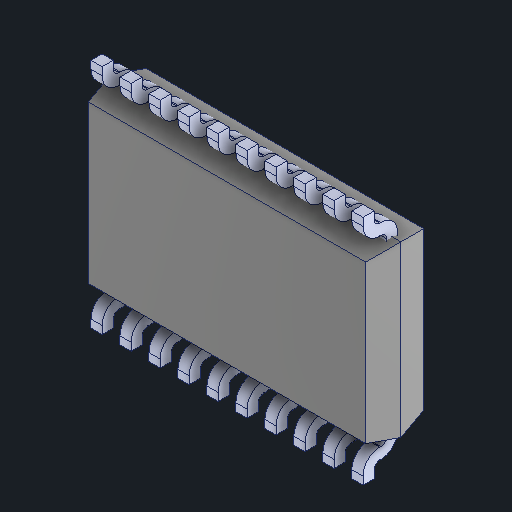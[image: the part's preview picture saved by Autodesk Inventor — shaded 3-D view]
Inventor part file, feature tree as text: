
AUTODESK INVENTOR PART (.ipt)
format: ipt  version: 2024 (Build 280153000, 153)  size: 306,688 bytes
history: native  units: mm
features: other x31, mirror x10, fillet x1
ambient origin geometry x8: Origin, YZ Plane, XZ Plane, XY Plane, X Axis, Y Axis, Z Axis, Center Point
bodies: Body1 (feature_tree), Body2 (feature_tree), Body3 (feature_tree), Body4 (feature_tree), Body5 (feature_tree), Body6 (feature_tree), Body7 (feature_tree), Body8 (feature_tree), Body9 (feature_tree), Body10 (feature_tree), Body11 (feature_tree), Body12 (feature_tree), Body13 (feature_tree), Body14 (feature_tree), Body15 (feature_tree), Body16 (feature_tree), Body17 (feature_tree), Body18 (feature_tree), Body19 (feature_tree), Body20 (feature_tree), Body21 (feature_tree)
feature tree (42):
  other  "Твердое тело1"
  other  "Твердое тело2"
  other  "Твердое тело3"
  other  "Твердое тело4"
  other  "Твердое тело5"
  other  "Твердое тело6"
  other  "Твердое тело7"
  other  "Твердое тело8"
  other  "Твердое тело9"
  other  "Твердое тело10"
  other  "Твердое тело11"
  other  "Твердое тело12"
  other  "Твердое тело13"
  other  "Твердое тело14"
  other  "Твердое тело15"
  other  "Твердое тело16"
  other  "Твердое тело17"
  other  "Твердое тело18"
  other  "Твердое тело19"
  other  "Твердое тело20"
  other  "Твердое тело21"
  other  "Boss-Extrude1"
  fillet  "Fillet2"  [1 undecoded]
  other  "LPattern2[1]"
  other  "LPattern2[2]"
  other  "LPattern2[3]"
  other  "LPattern2[4]"
  other  "LPattern2[5]"
  other  "LPattern2[6]"
  other  "LPattern2[7]"
  other  "LPattern2[8]"
  other  "LPattern2[9]"
  mirror  "Mirror2[1]"
  mirror  "Mirror2[2]"
  mirror  "Mirror2[3]"
  mirror  "Mirror2[4]"
  mirror  "Mirror2[5]"
  mirror  "Mirror2[6]"
  mirror  "Mirror2[7]"
  mirror  "Mirror2[8]"
  mirror  "Mirror2[9]"
  mirror  "Mirror2[10]"
note: 1 required parameter value undecoded (feature->parameter linkage not recoverable at this tier; creation-order binding heuristic only, values carry confidence <= 0.55)
